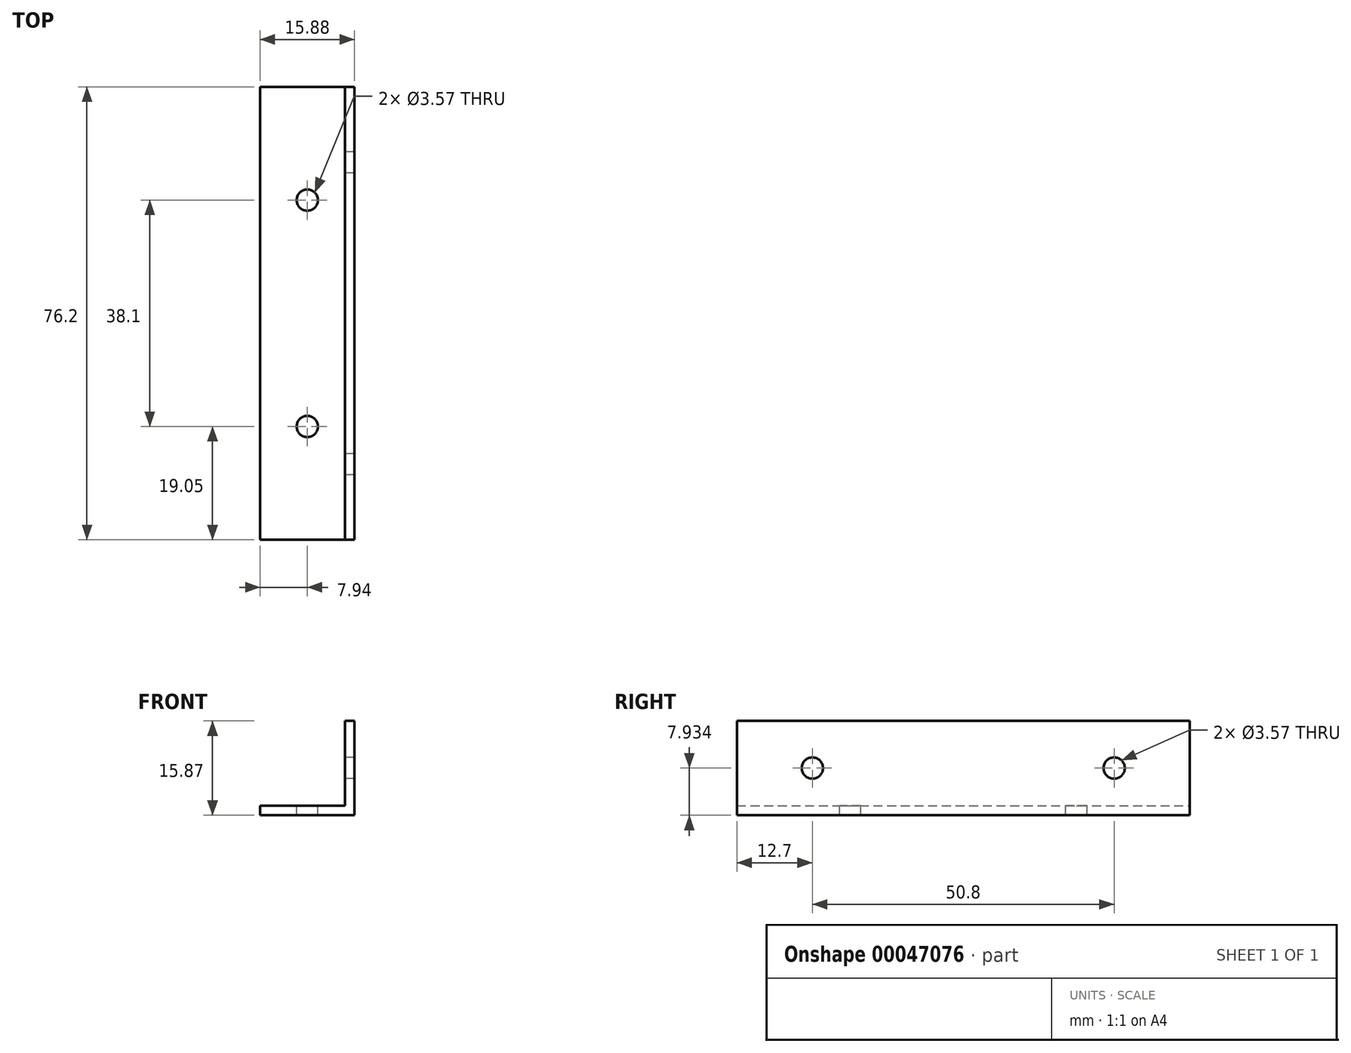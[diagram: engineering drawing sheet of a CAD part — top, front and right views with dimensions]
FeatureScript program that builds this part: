
annotation { "Feature Type Name" : "Feature", "Feature Type Description" : "" }
export const myFeature = defineFeature(function(context is Context, id is Id, definition is map)
    precondition{}
    {
        {
            var Q0;
            Q0=qCreatedBy(makeId("Front.planeOp"),FACE);
            var sketch = newSketch(context, id + "F0", { "sketchPlane" : qUnion([Q0])});
            skLineSegment(sketch, "E0.rect.bottom", {"start": v(7.94, 0.8) * mm, "end": v(-7.94, 0.8) * mm});
            skLineSegment(sketch, "E0.rect.top", {"start": v(7.94, -0.8) * mm, "end": v(-7.94, -0.8) * mm});
            skLineSegment(sketch, "E0.rect.left", {"start": v(7.94, 0.8) * mm, "end": v(7.94, -0.8) * mm});
            skLineSegment(sketch, "E0.rect.right", {"start": v(-7.94, 0.8) * mm, "end": v(-7.94, -0.8) * mm});
            skPoint(sketch, "E0.rect.middle", {"position": v(0, 0) * mm});
            skSolve(sketch);
        }
        {
            var Q0;
            Q0 = qSketchRegion(id + "F0", true);
            extrude(context, id + "F1", {"entities" : qUnion([Q0]), "endBound" : BoundingType.SYMMETRIC, "depth" : 76.2 * mm});
        }
        {
            var Q0;
            Q0=makeQuery(id+"F1.opExtrude","SWEPT_FACE",FACE,{"disambiguationData":[OSD([sQuery(id+"F0.wireOp",EDGE,"E0.rect.bottom")])]});
            var sketch = newSketch(context, id + "F2", { "sketchPlane" : qUnion([Q0])});
            skLineSegment(sketch, "E1.bottom", {"start": v(7.94, -38.1) * mm, "end": v(6.35, -38.1) * mm});
            skLineSegment(sketch, "E1.top", {"start": v(7.94, 38.1) * mm, "end": v(6.35, 38.1) * mm});
            skLineSegment(sketch, "E1.left", {"start": v(7.94, -38.1) * mm, "end": v(7.94, 38.1) * mm});
            skLineSegment(sketch, "E1.right", {"start": v(6.35, -38.1) * mm, "end": v(6.35, 38.1) * mm});
            skSolve(sketch);
        }
        {
            var Q0;
            Q0=makeQuery(id+"F2.imprint","IMPRINT",FACE,{"disambiguationData":[TD([[makeQuery(id+"F2.imprint","IMPRINT",EDGE,{"derivedFrom":sQuery(id+"F2.wireOp",EDGE,"E1.bottom")}),-1.0]])]});
            extrude(context, id + "F3", {"entities" : qUnion([Q0]), "operationType" : NewBodyOperationType.ADD, "depth" : 14.29 * mm});
        }
        {
            var Q0;
            Q0=makeQuery(id+"F3.opExtrude","SWEPT_FACE",FACE,{"disambiguationData":[OSD([sQuery(id+"F2.wireOp",EDGE,"E1.right")])]});
            var sketch = newSketch(context, id + "F4", { "sketchPlane" : qUnion([Q0])});
            skCircle(sketch, "E2", {"center": v(-25.4, 7.14) * mm, "radius": 1.79 * mm});
            skCircle(sketch, "E3.MirrorC", {"center": v(25.4, 7.14) * mm, "radius": 1.79 * mm});
            skSolve(sketch);
        }
        {
            var Q0;
            Q0 = qSketchRegion(id + "F4", true);
            extrude(context, id + "F5", {"entities" : qUnion([Q0]), "operationType" : NewBodyOperationType.REMOVE, "endBound" : BoundingType.THROUGH_ALL, "oppositeDirection" : true, "depth" : 25.4 * mm});
        }
        {
            var Q0;
            Q0=makeQuery(id+"F1.opExtrude","SWEPT_FACE",FACE,{"disambiguationData":[OSD([sQuery(id+"F0.wireOp",EDGE,"E0.rect.bottom")])]});
            var sketch = newSketch(context, id + "F6", { "sketchPlane" : qUnion([Q0])});
            skCircle(sketch, "E4", {"center": v(0, 19.05) * mm, "radius": 1.79 * mm});
            skCircle(sketch, "E5.MirrorC", {"center": v(0, -19.05) * mm, "radius": 1.79 * mm});
            skSolve(sketch);
        }
        {
            var Q0;
            Q0 = qSketchRegion(id + "F6", true);
            extrude(context, id + "F7", {"entities" : qUnion([Q0]), "operationType" : NewBodyOperationType.REMOVE, "endBound" : BoundingType.THROUGH_ALL, "oppositeDirection" : true, "depth" : 25.4 * mm});
        }
    });
